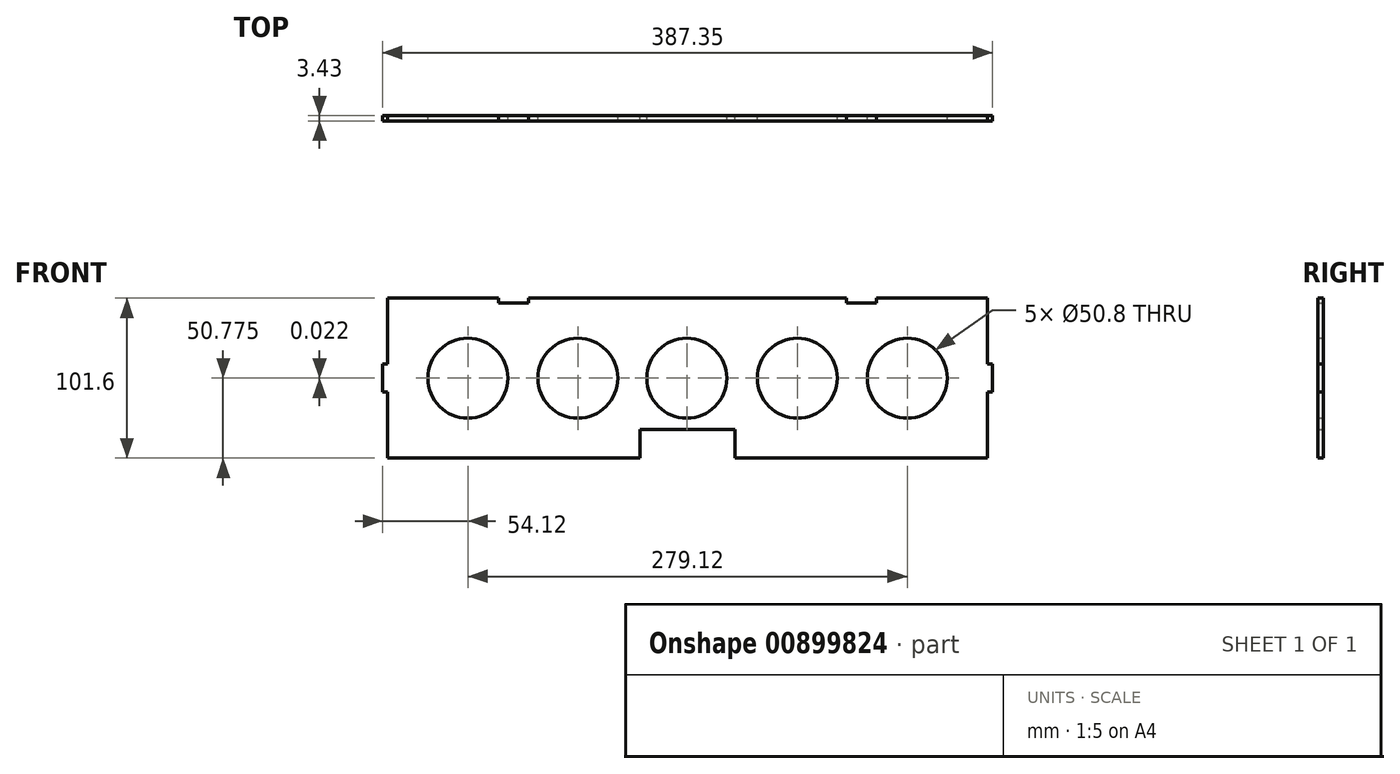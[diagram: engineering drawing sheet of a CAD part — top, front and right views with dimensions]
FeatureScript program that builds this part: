
annotation { "Feature Type Name" : "Feature", "Feature Type Description" : "" }
export const myFeature = defineFeature(function(context is Context, id is Id, definition is map)
    precondition{}
    {
        {
            var Q0;
            Q0=qCreatedBy(makeId("Front.planeOp"),FACE);
            var sketch = newSketch(context, id + "F0", { "sketchPlane" : qUnion([Q0])});
            skLineSegment(sketch, "E0", {"start": v(205.22, -7.2) * mm, "end": v(205.22, -4.02) * mm});
            skLineSegment(sketch, "E1", {"start": v(278.88, -45.93) * mm, "end": v(275.7, -45.93) * mm});
            skLineSegment(sketch, "E2", {"start": v(278.88, -63.71) * mm, "end": v(278.88, -45.93) * mm});
            skLineSegment(sketch, "E3", {"start": v(275.7, -63.71) * mm, "end": v(278.88, -63.71) * mm});
            skLineSegment(sketch, "E4", {"start": v(115.37, -105.62) * mm, "end": v(115.37, -87.46) * mm});
            skLineSegment(sketch, "E5", {"start": v(115.37, -87.46) * mm, "end": v(55.05, -87.46) * mm});
            skLineSegment(sketch, "E6", {"start": v(55.05, -87.46) * mm, "end": v(55.05, -105.62) * mm});
            skLineSegment(sketch, "E7", {"start": v(-108.47, -63.71) * mm, "end": v(-105.3, -63.71) * mm});
            skLineSegment(sketch, "E8", {"start": v(-108.47, -45.93) * mm, "end": v(-108.47, -63.71) * mm});
            skLineSegment(sketch, "E9", {"start": v(-105.3, -45.93) * mm, "end": v(-108.47, -45.93) * mm});
            skLineSegment(sketch, "E10", {"start": v(-34.8, -4.02) * mm, "end": v(-34.8, -7.2) * mm});
            skLineSegment(sketch, "E11", {"start": v(-34.8, -7.2) * mm, "end": v(-15.76, -7.2) * mm});
            skLineSegment(sketch, "E12", {"start": v(-15.76, -7.2) * mm, "end": v(-15.76, -4.02) * mm});
            skLineSegment(sketch, "E13", {"start": v(186.17, -4.02) * mm, "end": v(186.17, -7.2) * mm});
            skLineSegment(sketch, "E14", {"start": v(186.17, -7.2) * mm, "end": v(205.22, -7.2) * mm});
            skCircle(sketch, "E15", {"center": v(84.71, -54.84) * mm, "radius": 25.4 * mm});
            skCircle(sketch, "E16", {"center": v(154.93, -54.82) * mm, "radius": 25.4 * mm});
            skCircle(sketch, "E17", {"center": v(224.77, -54.82) * mm, "radius": 25.4 * mm});
            skCircle(sketch, "E18", {"center": v(-54.35, -54.82) * mm, "radius": 25.4 * mm});
            skCircle(sketch, "E19", {"center": v(15.49, -54.82) * mm, "radius": 25.4 * mm});
            skLineSegment(sketch, "E20", {"start": v(-105.3, -105.62) * mm, "end": v(55.05, -105.62) * mm});
            skLineSegment(sketch, "E21", {"start": v(-105.3, -63.71) * mm, "end": v(-105.3, -105.62) * mm});
            skLineSegment(sketch, "E22", {"start": v(-34.8, -4.02) * mm, "end": v(-105.3, -4.02) * mm});
            skLineSegment(sketch, "E23", {"start": v(275.7, -105.62) * mm, "end": v(275.7, -63.71) * mm});
            skLineSegment(sketch, "E24", {"start": v(115.37, -105.62) * mm, "end": v(275.7, -105.62) * mm});
            skLineSegment(sketch, "E25", {"start": v(-105.3, -4.02) * mm, "end": v(-105.3, -45.93) * mm});
            skLineSegment(sketch, "E26", {"start": v(275.7, -45.93) * mm, "end": v(275.7, -4.02) * mm});
            skLineSegment(sketch, "E27", {"start": v(275.7, -4.02) * mm, "end": v(205.22, -4.02) * mm});
            skLineSegment(sketch, "E28", {"start": v(186.17, -4.02) * mm, "end": v(-15.76, -4.02) * mm});
            skSolve(sketch);
        }
        {
            var Q0;
            Q0 = qSketchRegion(id + "F0", true);
            extrude(context, id + "F1", {"entities" : qUnion([Q0]), "depth" : 3.43 * mm, "offsetDistance" : 25.4 * mm});
        }
    });
